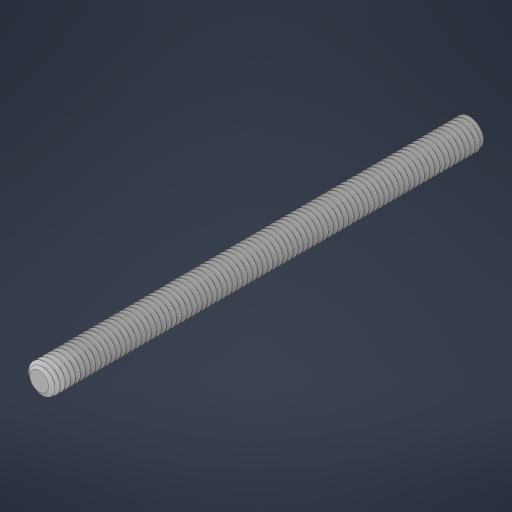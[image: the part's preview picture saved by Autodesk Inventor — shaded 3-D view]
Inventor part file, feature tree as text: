
AUTODESK INVENTOR PART (.ipt)
format: ipt  version: 2023 (Build 270158000, 158)  size: 2,135,552 bytes
history: native  units: in
note: dims shown in document units (in); Inventor stores cm internally (conversion verified against a paired STEP export)
features: mirror x1
ambient origin geometry x8: Origin, YZ Plane, XZ Plane, XY Plane, X Axis, Y Axis, Z Axis, Center Point
bodies: Solid1 (feature_tree)
feature tree (1):
  mirror  "Mirror1"
